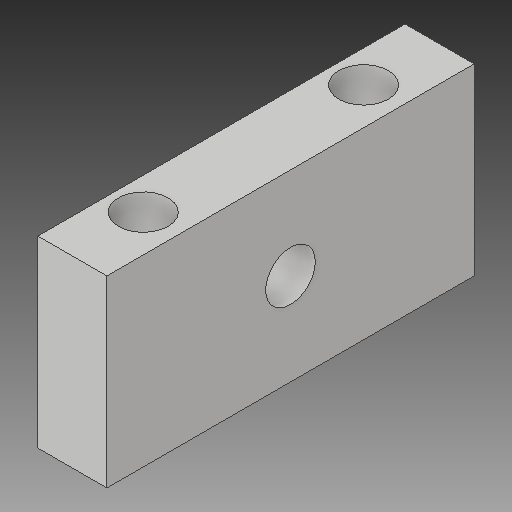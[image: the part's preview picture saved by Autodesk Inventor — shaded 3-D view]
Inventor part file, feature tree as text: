
AUTODESK INVENTOR PART (.ipt)
format: ipt  version: 2019 (Build 230136000, 136)  size: 112,128 bytes
history: native  units: in
note: dims shown in document units (in); Inventor stores cm internally (conversion verified against a paired STEP export)
features: sketch x3, hole x2, other x1, extrude x1
ambient origin geometry x8: Origin, YZ Plane, XZ Plane, XY Plane, X Axis, Y Axis, Z Axis, Center Point
bodies: Solid1 (feature_tree)
feature tree (7):
  other  "WheelIntakeSpringStop"
  extrude  "Extrusion1"  Depth=1.0in
  hole  "Hole1"  [1 undecoded]
  hole  "Hole2"  [1 undecoded]
  sketch  "Sketch1"  dims[d0=0.5in d1=1.0in]
  sketch  "Sketch2"  dims[d2=0.188in d3=0.0in]
  sketch  "Sketch3"  dims[d4=0.135in d5=0.2in d6=0.375in d7=0.25in d8=0.5635in d9=0.25in d10=0.8108in d11=0.5in d12=1.0in d13=0.25in d14=0.5in d15=0.135in d16=0.276in d17=0.375in d18=0.25in d19=0.5635in d20=0.432in d21=0.8108in d22=0.2in d23=0.2in]
note: 2 required parameter values undecoded (feature->parameter linkage not recoverable at this tier; creation-order binding heuristic only, values carry confidence <= 0.55)
